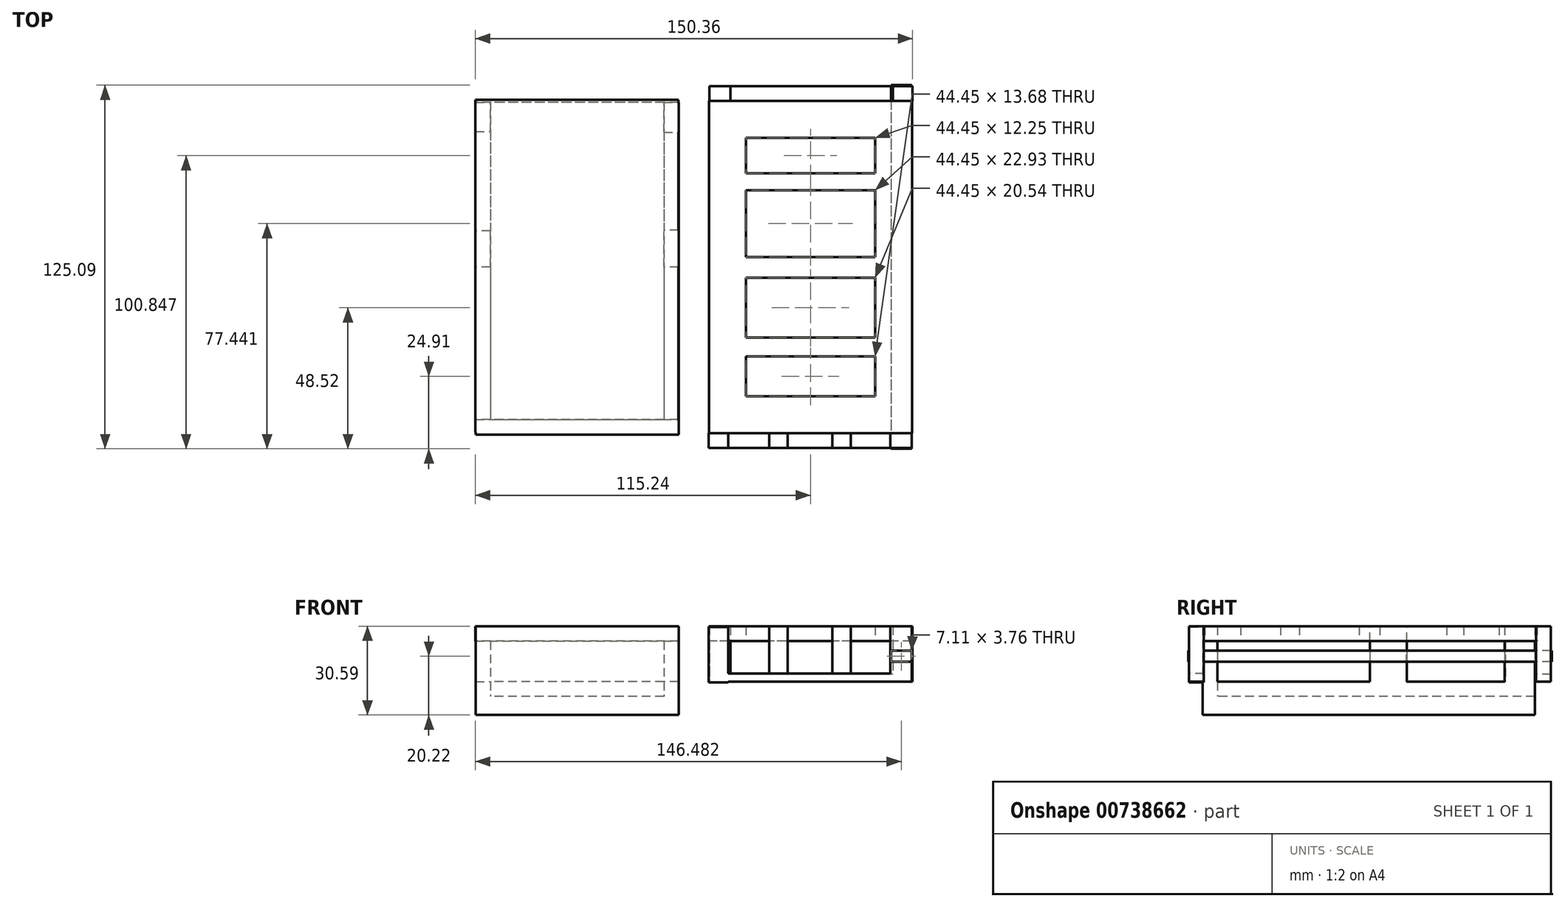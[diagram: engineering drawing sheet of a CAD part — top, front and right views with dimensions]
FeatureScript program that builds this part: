
annotation { "Feature Type Name" : "Feature", "Feature Type Description" : "" }
export const myFeature = defineFeature(function(context is Context, id is Id, definition is map)
    precondition{}
    {
        {
            var Q0;
            Q0=qCreatedBy(makeId("Top.planeOp"),FACE);
            var sketch = newSketch(context, id + "F0", { "sketchPlane" : qUnion([Q0])});
            skLineSegment(sketch, "E0.bottom", {"start": v(-45.39, 57.49) * mm, "end": v(-115.24, 57.49) * mm});
            skLineSegment(sketch, "E0.top", {"start": v(-45.39, -56.81) * mm, "end": v(-115.24, -56.81) * mm});
            skLineSegment(sketch, "E0.left", {"start": v(-45.39, 57.49) * mm, "end": v(-45.39, -56.81) * mm});
            skLineSegment(sketch, "E0.right", {"start": v(-115.24, 57.49) * mm, "end": v(-115.24, -56.81) * mm});
            skSolve(sketch);
        }
        {
            var Q0;
            Q0 = qSketchRegion(id + "F0", true);
            extrude(context, id + "F1", {"entities" : qUnion([Q0]), "depth" : 5.08 * mm, "offsetDistance" : 25.4 * mm});
        }
        {
            var Q0;
            Q0=qCreatedBy(makeId("Top.planeOp"),FACE);
            cPlane(context, id + "F2", {"entities" : qUnion([Q0]), "cplaneType" : CPlaneType.OFFSET, "offset" : 25.4 * mm, "oppositeDirection" : true, "width" : 152.4 * mm, "height" : 152.4 * mm});
        }
        {
            var Q0;
            Q0=qCreatedBy(id+"F2.planeOp",FACE);
            var sketch = newSketch(context, id + "F3", { "sketchPlane" : qUnion([Q0])});
            skLineSegment(sketch, "E1.bottom", {"start": v(-45.35, -57.6) * mm, "end": v(-115.2, -57.6) * mm});
            skLineSegment(sketch, "E1.top", {"start": v(-45.35, 56.7) * mm, "end": v(-115.2, 56.7) * mm});
            skLineSegment(sketch, "E1.left", {"start": v(-45.35, -57.6) * mm, "end": v(-45.35, 56.7) * mm});
            skLineSegment(sketch, "E1.right", {"start": v(-115.2, -57.6) * mm, "end": v(-115.2, 56.7) * mm});
            skSolve(sketch);
        }
        {
            var Q0;
            Q0 = qSketchRegion(id + "F3", true);
            extrude(context, id + "F4", {"entities" : qUnion([Q0]), "depth" : 6.35 * mm, "offsetDistance" : 25.4 * mm});
        }
        {
            var Q0;
            Q0=qCreatedBy(makeId("Front.planeOp"),FACE);
            cPlane(context, id + "F5", {"entities" : qUnion([Q0]), "cplaneType" : CPlaneType.OFFSET, "offset" : 57.15 * mm, "width" : 152.4 * mm, "height" : 152.4 * mm});
        }
        {
            var Q0;
            Q0=qCreatedBy(makeId("Right.planeOp"),FACE);
            cPlane(context, id + "F6", {"entities" : qUnion([Q0]), "cplaneType" : CPlaneType.OFFSET, "offset" : 50.8 * mm, "oppositeDirection" : true, "width" : 152.4 * mm, "height" : 152.4 * mm});
        }
        {
            var Q0;
            Q0=qCreatedBy(makeId("Top.planeOp"),FACE);
            var sketch = newSketch(context, id + "F7", { "sketchPlane" : qUnion([Q0])});
            skLineSegment(sketch, "E2.bottom", {"start": v(34.93, -57.15) * mm, "end": v(-34.93, -57.15) * mm});
            skLineSegment(sketch, "E2.top", {"start": v(34.93, 57.15) * mm, "end": v(-34.92, 57.15) * mm});
            skLineSegment(sketch, "E2.left", {"start": v(34.93, -57.15) * mm, "end": v(34.93, 57.15) * mm});
            skLineSegment(sketch, "E2.right", {"start": v(-34.93, -57.15) * mm, "end": v(-34.92, 57.15) * mm});
            skPoint(sketch, "E2.middle", {"position": v(0, 0) * mm});
            skLineSegment(sketch, "E3", {"start": v(-22.22, 57.15) * mm, "end": v(-22.22, -57.15) * mm});
            skLineSegment(sketch, "E4", {"start": v(22.22, 57.15) * mm, "end": v(22.23, -57.15) * mm});
            skLineSegment(sketch, "E5", {"start": v(-34.92, 44.45) * mm, "end": v(34.93, 44.45) * mm});
            skLineSegment(sketch, "E6", {"start": v(-34.93, -44.45) * mm, "end": v(34.93, -44.45) * mm});
            skLineSegment(sketch, "E7", {"start": v(-22.22, 32.2) * mm, "end": v(22.22, 32.2) * mm});
            skLineSegment(sketch, "E8", {"start": v(-22.22, 26.39) * mm, "end": v(22.22, 26.39) * mm});
            skLineSegment(sketch, "E9", {"start": v(-22.22, 3.46) * mm, "end": v(22.22, 3.46) * mm});
            skLineSegment(sketch, "E10", {"start": v(-22.22, -3.73) * mm, "end": v(22.22, -3.73) * mm});
            skLineSegment(sketch, "E11", {"start": v(-22.22, -24.27) * mm, "end": v(22.23, -24.27) * mm});
            skLineSegment(sketch, "E12", {"start": v(-22.22, -30.77) * mm, "end": v(22.23, -30.77) * mm});
            skSolve(sketch);
        }
        {
            var Q0;
            Q0 = qSketchRegion(id + "F7", true);
            var Q1;
            {var subQ0=sQuery(id+"F7.wireOp",EDGE,"E7");Q1=makeQuery(id+"F7.imprint","IMPRINT",FACE,{"disambiguationData":[TD([[makeQuery(id+"F7.imprint","IMPRINT",EDGE,{"derivedFrom":subQ0}),-1.0]])]});}
            var Q2;
            {var subQ0=sQuery(id+"F7.wireOp",EDGE,"E9");Q2=makeQuery(id+"F7.imprint","IMPRINT",FACE,{"disambiguationData":[TD([[makeQuery(id+"F7.imprint","IMPRINT",EDGE,{"derivedFrom":subQ0}),-1.0]])]});}
            var Q3;
            {var subQ0=sQuery(id+"F7.wireOp",EDGE,"E11");Q3=makeQuery(id+"F7.imprint","IMPRINT",FACE,{"disambiguationData":[TD([[makeQuery(id+"F7.imprint","IMPRINT",EDGE,{"derivedFrom":subQ0}),-1.0]])]});}
            extrude(context, id + "F8", {"entities" : qUnion([Q0, Q1, Q2, Q3]), "depth" : 5.08 * mm, "offsetDistance" : 25.4 * mm});
        }
        {
            var Q0;
            Q0=qCreatedBy(id+"F5.planeOp",FACE);
            var sketch = newSketch(context, id + "F9", { "sketchPlane" : qUnion([Q0])});
            skLineSegment(sketch, "E13.bottom", {"start": v(-35, 4.9) * mm, "end": v(-28.26, 4.9) * mm});
            skLineSegment(sketch, "E13.top", {"start": v(-35, -14.16) * mm, "end": v(-28.26, -14.16) * mm});
            skLineSegment(sketch, "E13.left", {"start": v(-35, 4.9) * mm, "end": v(-35, -14.16) * mm});
            skLineSegment(sketch, "E13.right", {"start": v(-28.26, 4.9) * mm, "end": v(-28.26, -14.16) * mm});
            skLineSegment(sketch, "E14.bottom", {"start": v(34.85, 5.13) * mm, "end": v(27.5, 5.13) * mm});
            skLineSegment(sketch, "E14.top", {"start": v(34.85, -13.92) * mm, "end": v(27.5, -13.92) * mm});
            skLineSegment(sketch, "E14.left", {"start": v(34.85, 5.13) * mm, "end": v(34.85, -13.92) * mm});
            skLineSegment(sketch, "E14.right", {"start": v(27.5, 5.13) * mm, "end": v(27.5, -13.92) * mm});
            skLineSegment(sketch, "E15.bottom", {"start": v(34.85, -13.92) * mm, "end": v(-35, -13.92) * mm});
            skLineSegment(sketch, "E15.top", {"start": v(34.85, -11.15) * mm, "end": v(-35, -11.15) * mm});
            skLineSegment(sketch, "E15.left", {"start": v(34.85, -13.92) * mm, "end": v(34.85, -11.15) * mm});
            skLineSegment(sketch, "E15.right", {"start": v(-35, -13.92) * mm, "end": v(-35, -11.15) * mm});
            skSolve(sketch);
        }
        {
            var Q0;
            Q0 = qSketchRegion(id + "F9", true);
            extrude(context, id + "F10", {"entities" : qUnion([Q0]), "operationType" : NewBodyOperationType.ADD, "depth" : 5.08 * mm, "offsetDistance" : 25.4 * mm});
        }
        {
            var Q0;
            Q0=makeQuery(id+"F8.opExtrude","SWEPT_FACE",FACE,{"disambiguationData":[OSD([sQuery(id+"F7.wireOp",EDGE,"E2.top")])]});
            var sketch = newSketch(context, id + "F11", { "sketchPlane" : qUnion([Q0])});
            skLineSegment(sketch, "E16.bottom", {"start": v(34.73, 5.19) * mm, "end": v(27.49, 5.19) * mm});
            skLineSegment(sketch, "E16.top", {"start": v(34.73, -13.86) * mm, "end": v(27.49, -13.86) * mm});
            skLineSegment(sketch, "E16.left", {"start": v(34.73, 5.19) * mm, "end": v(34.73, -13.86) * mm});
            skLineSegment(sketch, "E16.right", {"start": v(27.49, 5.19) * mm, "end": v(27.49, -13.86) * mm});
            skLineSegment(sketch, "E17.bottom", {"start": v(-35.12, 5.19) * mm, "end": v(-28.3, 5.19) * mm});
            skLineSegment(sketch, "E17.top", {"start": v(-35.12, -13.86) * mm, "end": v(-28.3, -13.86) * mm});
            skLineSegment(sketch, "E17.left", {"start": v(-35.12, 5.19) * mm, "end": v(-35.12, -13.86) * mm});
            skLineSegment(sketch, "E17.right", {"start": v(-28.3, 5.19) * mm, "end": v(-28.3, -13.86) * mm});
            skLineSegment(sketch, "E18.bottom", {"start": v(-35.12, -13.86) * mm, "end": v(34.73, -13.86) * mm});
            skLineSegment(sketch, "E18.top", {"start": v(-35.12, -11.32) * mm, "end": v(34.73, -11.32) * mm});
            skLineSegment(sketch, "E18.left", {"start": v(-35.12, -13.86) * mm, "end": v(-35.12, -11.32) * mm});
            skLineSegment(sketch, "E18.right", {"start": v(34.73, -13.86) * mm, "end": v(34.73, -11.32) * mm});
            skSolve(sketch);
        }
        {
            var Q0;
            Q0 = qSketchRegion(id + "F11", true);
            extrude(context, id + "F12", {"entities" : qUnion([Q0]), "operationType" : NewBodyOperationType.ADD, "depth" : 5.08 * mm, "offsetDistance" : 25.4 * mm});
        }
        {
            var Q0;
            Q0=makeQuery(id+"F4.opExtrude","CAP_FACE",FACE,{"disambiguationData":[OSD([sQuery(id+"F3.wireOp",EDGE,"E1.bottom"),sQuery(id+"F3.wireOp",EDGE,"E1.top"),sQuery(id+"F3.wireOp",EDGE,"E1.left"),sQuery(id+"F3.wireOp",EDGE,"E1.right")])],"isStart":false});
            var sketch = newSketch(context, id + "F13", { "sketchPlane" : qUnion([Q0])});
            skLineSegment(sketch, "E19.bottom", {"start": v(-115.2, 56.7) * mm, "end": v(-110.12, 56.7) * mm});
            skLineSegment(sketch, "E19.top", {"start": v(-115.2, -57.6) * mm, "end": v(-110.12, -57.6) * mm});
            skLineSegment(sketch, "E19.left", {"start": v(-115.2, 56.7) * mm, "end": v(-115.2, -57.6) * mm});
            skLineSegment(sketch, "E19.right", {"start": v(-110.12, 56.7) * mm, "end": v(-110.12, -57.6) * mm});
            skLineSegment(sketch, "E20.bottom", {"start": v(-45.35, 56.7) * mm, "end": v(-50.43, 56.7) * mm});
            skLineSegment(sketch, "E20.top", {"start": v(-45.35, -57.6) * mm, "end": v(-50.43, -57.6) * mm});
            skLineSegment(sketch, "E20.left", {"start": v(-45.35, 56.7) * mm, "end": v(-45.35, -57.6) * mm});
            skLineSegment(sketch, "E20.right", {"start": v(-50.43, 56.7) * mm, "end": v(-50.43, -57.6) * mm});
            skLineSegment(sketch, "E21.bottom", {"start": v(-50.43, -57.6) * mm, "end": v(-110.12, -57.6) * mm});
            skLineSegment(sketch, "E21.top", {"start": v(-50.43, -52.53) * mm, "end": v(-110.12, -52.53) * mm});
            skLineSegment(sketch, "E21.left", {"start": v(-50.43, -57.6) * mm, "end": v(-50.43, -52.53) * mm});
            skLineSegment(sketch, "E21.right", {"start": v(-110.12, -57.6) * mm, "end": v(-110.12, -52.53) * mm});
            skLineSegment(sketch, "E22.bottom", {"start": v(-50.43, 56.7) * mm, "end": v(-110.12, 56.7) * mm});
            skLineSegment(sketch, "E22.top", {"start": v(-50.43, 51.61) * mm, "end": v(-110.12, 51.61) * mm});
            skLineSegment(sketch, "E22.left", {"start": v(-50.43, 56.7) * mm, "end": v(-50.43, 51.61) * mm});
            skLineSegment(sketch, "E22.right", {"start": v(-110.12, 56.7) * mm, "end": v(-110.12, 51.61) * mm});
            skLineSegment(sketch, "E23", {"start": v(-110.12, 51.61) * mm, "end": v(-115.2, 51.61) * mm});
            skLineSegment(sketch, "E24", {"start": v(-50.43, 51.61) * mm, "end": v(-45.35, 51.61) * mm});
            skLineSegment(sketch, "E25", {"start": v(-110.12, -52.53) * mm, "end": v(-115.2, -52.53) * mm});
            skLineSegment(sketch, "E26", {"start": v(-50.43, -52.53) * mm, "end": v(-45.35, -52.53) * mm});
            skLineSegment(sketch, "E27", {"start": v(-45.35, 0) * mm, "end": v(-115.2, 0) * mm, "construction": true});
            skSolve(sketch);
        }
        {
            var Q0;
            {var subQ0=sQuery(id+"F13.wireOp",EDGE,"E19.bottom");Q0=makeQuery(id+"F13.imprint","IMPRINT",FACE,{"disambiguationData":[TD([[makeQuery(id+"F13.imprint","IMPRINT",EDGE,{"derivedFrom":subQ0}),1.0]])]});}
            var Q1;
            {var subQ0=sQuery(id+"F13.wireOp",EDGE,"E19.top");Q1=makeQuery(id+"F13.imprint","IMPRINT",FACE,{"disambiguationData":[TD([[makeQuery(id+"F13.imprint","IMPRINT",EDGE,{"derivedFrom":subQ0}),-1.0]])]});}
            var Q2;
            {var subQ0=sQuery(id+"F13.wireOp",EDGE,"E20.bottom");Q2=makeQuery(id+"F13.imprint","IMPRINT",FACE,{"disambiguationData":[TD([[makeQuery(id+"F13.imprint","IMPRINT",EDGE,{"derivedFrom":subQ0}),1.0]])]});}
            var Q3;
            {var subQ0=sQuery(id+"F13.wireOp",EDGE,"E20.top");Q3=makeQuery(id+"F13.imprint","IMPRINT",FACE,{"disambiguationData":[TD([[makeQuery(id+"F13.imprint","IMPRINT",EDGE,{"derivedFrom":subQ0}),-1.0]])]});}
            var Q4;
            Q4=makeQuery(id+"F13.imprint","IMPRINT",FACE,{"disambiguationData":[TD([[makeQuery(id+"F13.imprint","IMPRINT",EDGE,{"derivedFrom":sQuery(id+"F13.wireOp",EDGE,"E19.right")}),-1.0]])]});
            var Q5;
            Q5=makeQuery(id+"F13.imprint","IMPRINT",FACE,{"disambiguationData":[TD([[makeQuery(id+"F13.imprint","IMPRINT",EDGE,{"derivedFrom":sQuery(id+"F13.wireOp",EDGE,"E20.right")}),1.0]])]});
            var Q6;
            Q6=makeQuery(id+"F13.imprint","IMPRINT",FACE,{"disambiguationData":[TD([[makeQuery(id+"F13.imprint","IMPRINT",EDGE,{"derivedFrom":sQuery(id+"F13.wireOp",EDGE,"E21.bottom")}),-1.0]])]});
            extrude(context, id + "F14", {"entities" : qUnion([Q0, Q1, Q2, Q3, Q4, Q5, Q6]), "operationType" : NewBodyOperationType.ADD, "depth" : 5.08 * mm, "offsetDistance" : 25.4 * mm});
        }
        {
            var Q0;
            Q0=makeQuery(id+"F14.opExtrude","CAP_FACE",FACE,{"disambiguationData":[OSD([sQuery(id+"F13.wireOp",EDGE,"E19.bottom"),sQuery(id+"F13.wireOp",EDGE,"E19.top"),sQuery(id+"F13.wireOp",EDGE,"E19.left"),sQuery(id+"F13.wireOp",EDGE,"E19.right"),sQuery(id+"F13.wireOp",EDGE,"E20.bottom"),sQuery(id+"F13.wireOp",EDGE,"E20.top"),sQuery(id+"F13.wireOp",EDGE,"E20.left"),sQuery(id+"F13.wireOp",EDGE,"E20.right"),sQuery(id+"F13.wireOp",EDGE,"E21.bottom"),sQuery(id+"F13.wireOp",EDGE,"E21.top"),sQuery(id+"F13.wireOp",EDGE,"E22.left"),sQuery(id+"F13.wireOp",EDGE,"E22.right")])],"isStart":false});
            var sketch = newSketch(context, id + "F15", { "sketchPlane" : qUnion([Q0])});
            skLineSegment(sketch, "E28.bottom", {"start": v(-45.35, -57.6) * mm, "end": v(-115.2, -57.6) * mm});
            skLineSegment(sketch, "E28.top", {"start": v(-45.35, -52.5) * mm, "end": v(-115.2, -52.5) * mm});
            skLineSegment(sketch, "E28.left", {"start": v(-45.35, -57.6) * mm, "end": v(-45.35, -52.5) * mm});
            skLineSegment(sketch, "E28.right", {"start": v(-115.2, -57.6) * mm, "end": v(-115.2, -52.5) * mm});
            skLineSegment(sketch, "E29.bottom", {"start": v(-115.2, 12.39) * mm, "end": v(-110.12, 12.39) * mm});
            skLineSegment(sketch, "E29.top", {"start": v(-115.2, 0) * mm, "end": v(-110.12, 0) * mm});
            skLineSegment(sketch, "E29.left", {"start": v(-115.2, 12.39) * mm, "end": v(-115.2, 0) * mm});
            skLineSegment(sketch, "E29.right", {"start": v(-110.12, 12.39) * mm, "end": v(-110.12, 0) * mm});
            skLineSegment(sketch, "E30.bottom", {"start": v(-50.43, 12.63) * mm, "end": v(-45.35, 12.63) * mm});
            skLineSegment(sketch, "E30.top", {"start": v(-50.43, 0) * mm, "end": v(-45.35, 0) * mm});
            skLineSegment(sketch, "E30.left", {"start": v(-50.43, 12.63) * mm, "end": v(-50.43, 0) * mm});
            skLineSegment(sketch, "E30.right", {"start": v(-45.35, 12.63) * mm, "end": v(-45.35, 0) * mm});
            skLineSegment(sketch, "E31.bottom", {"start": v(-110.12, 56.7) * mm, "end": v(-115.2, 56.7) * mm});
            skLineSegment(sketch, "E31.top", {"start": v(-110.12, 46.55) * mm, "end": v(-115.2, 46.55) * mm});
            skLineSegment(sketch, "E31.left", {"start": v(-110.12, 56.7) * mm, "end": v(-110.12, 46.55) * mm});
            skLineSegment(sketch, "E31.right", {"start": v(-115.2, 56.7) * mm, "end": v(-115.2, 46.55) * mm});
            skLineSegment(sketch, "E32.bottom", {"start": v(-45.35, 56.7) * mm, "end": v(-50.43, 56.7) * mm});
            skLineSegment(sketch, "E32.top", {"start": v(-45.35, 46.38) * mm, "end": v(-50.43, 46.38) * mm});
            skLineSegment(sketch, "E32.left", {"start": v(-45.35, 56.7) * mm, "end": v(-45.35, 46.38) * mm});
            skLineSegment(sketch, "E32.right", {"start": v(-50.43, 56.7) * mm, "end": v(-50.43, 46.38) * mm});
            skSolve(sketch);
        }
        {
            var Q0;
            Q0 = qSketchRegion(id + "F15", true);
            extrude(context, id + "F16", {"entities" : qUnion([Q0]), "operationType" : NewBodyOperationType.ADD, "depth" : 19.05 * mm, "offsetDistance" : 25.4 * mm});
        }
        {
            var Q0;
            Q0=qCreatedBy(makeId("Right.planeOp"),FACE);
            cPlane(context, id + "F17", {"entities" : qUnion([Q0]), "cplaneType" : CPlaneType.OFFSET, "offset" : 27.7 * mm, "width" : 152.4 * mm, "height" : 152.4 * mm});
        }
        {
            var Q0;
            Q0=qCreatedBy(id+"F17.planeOp",FACE);
            var sketch = newSketch(context, id + "F18", { "sketchPlane" : qUnion([Q0])});
            skLineSegment(sketch, "E33.bottom", {"start": v(62.57, -3.3) * mm, "end": v(-62.52, -3.3) * mm});
            skLineSegment(sketch, "E33.top", {"start": v(62.57, -7.06) * mm, "end": v(-62.52, -7.06) * mm});
            skLineSegment(sketch, "E33.left", {"start": v(62.57, -3.3) * mm, "end": v(62.57, -7.06) * mm});
            skLineSegment(sketch, "E33.right", {"start": v(-62.52, -3.3) * mm, "end": v(-62.52, -7.06) * mm});
            skSolve(sketch);
        }
        {
            var Q0;
            Q0 = qSketchRegion(id + "F18", true);
            extrude(context, id + "F19", {"entities" : qUnion([Q0]), "operationType" : NewBodyOperationType.ADD, "depth" : 7.11 * mm, "offsetDistance" : 25.4 * mm});
        }
        {
            var Q0;
            Q0=makeQuery(id+"F10.opExtrude","CAP_FACE",FACE,{"disambiguationData":[OSD([sQuery(id+"F9.wireOp",EDGE,"E13.bottom"),sQuery(id+"F9.wireOp",EDGE,"E13.top"),sQuery(id+"F9.wireOp",EDGE,"E13.left"),sQuery(id+"F9.wireOp",EDGE,"E13.right"),sQuery(id+"F9.wireOp",EDGE,"E14.bottom"),sQuery(id+"F9.wireOp",EDGE,"E14.left"),sQuery(id+"F9.wireOp",EDGE,"E14.right"),sQuery(id+"F9.wireOp",EDGE,"E15.bottom"),sQuery(id+"F9.wireOp",EDGE,"E15.top"),sQuery(id+"F9.wireOp",EDGE,"E15.left"),sQuery(id+"F9.wireOp",EDGE,"E15.right")])],"isStart":false});
            var sketch = newSketch(context, id + "F20", { "sketchPlane" : qUnion([Q0])});
            skLineSegment(sketch, "E34.bottom", {"start": v(0, 5.1) * mm, "end": v(0, 5.1) * mm});
            skLineSegment(sketch, "E34.top", {"start": v(0, -13.92) * mm, "end": v(0, -13.92) * mm});
            skLineSegment(sketch, "E34.left", {"start": v(0, 5.1) * mm, "end": v(0, -13.92) * mm, "construction": true});
            skLineSegment(sketch, "E34.right", {"start": v(0, 5.1) * mm, "end": v(0, -13.92) * mm, "construction": true});
            skLineSegment(sketch, "E35.bottom", {"start": v(-28.26, -13.92) * mm, "end": v(0, -13.92) * mm, "construction": true});
            skLineSegment(sketch, "E35.top", {"start": v(-28.26, -13.92) * mm, "end": v(0, -13.92) * mm, "construction": true});
            skLineSegment(sketch, "E35.left", {"start": v(-28.26, -13.92) * mm, "end": v(-28.26, -13.92) * mm});
            skLineSegment(sketch, "E36.bottom", {"start": v(27.69, -13.92) * mm, "end": v(0, -13.92) * mm, "construction": true});
            skLineSegment(sketch, "E36.top", {"start": v(27.69, -13.92) * mm, "end": v(0, -13.92) * mm, "construction": true});
            skLineSegment(sketch, "E36.left", {"start": v(27.69, -13.92) * mm, "end": v(27.69, -13.92) * mm});
            skLineSegment(sketch, "E37.bottom", {"start": v(-14.13, -13.92) * mm, "end": v(-7.78, -13.92) * mm});
            skLineSegment(sketch, "E37.top", {"start": v(-14.13, 5.13) * mm, "end": v(-7.78, 5.13) * mm});
            skLineSegment(sketch, "E37.left", {"start": v(-14.13, -13.92) * mm, "end": v(-14.13, 5.13) * mm});
            skLineSegment(sketch, "E37.right", {"start": v(-7.78, -13.92) * mm, "end": v(-7.78, 5.13) * mm});
            skLineSegment(sketch, "E38.bottom", {"start": v(13.84, -13.92) * mm, "end": v(7.5, -13.92) * mm});
            skLineSegment(sketch, "E38.top", {"start": v(13.84, 5.13) * mm, "end": v(7.5, 5.13) * mm});
            skLineSegment(sketch, "E38.left", {"start": v(13.84, -13.92) * mm, "end": v(13.84, 5.13) * mm});
            skLineSegment(sketch, "E38.right", {"start": v(7.5, -13.92) * mm, "end": v(7.5, 5.13) * mm});
            skSolve(sketch);
        }
        {
            var Q0;
            {var subQ0=sQuery(id+"F20.wireOp",EDGE,"E37.top");Q0=makeQuery(id+"F20.imprint","IMPRINT",FACE,{"disambiguationData":[TD([[makeQuery(id+"F20.imprint","IMPRINT",EDGE,{"derivedFrom":subQ0}),-1.0]])]});}
            var Q1;
            {var subQ0=sQuery(id+"F20.wireOp",EDGE,"E38.top");Q1=makeQuery(id+"F20.imprint","IMPRINT",FACE,{"disambiguationData":[TD([[makeQuery(id+"F20.imprint","IMPRINT",EDGE,{"derivedFrom":subQ0}),1.0]])]});}
            extrude(context, id + "F21", {"entities" : qUnion([Q0, Q1]), "oppositeDirection" : true, "depth" : 5.08 * mm, "offsetDistance" : 25.4 * mm});
        }
    });
